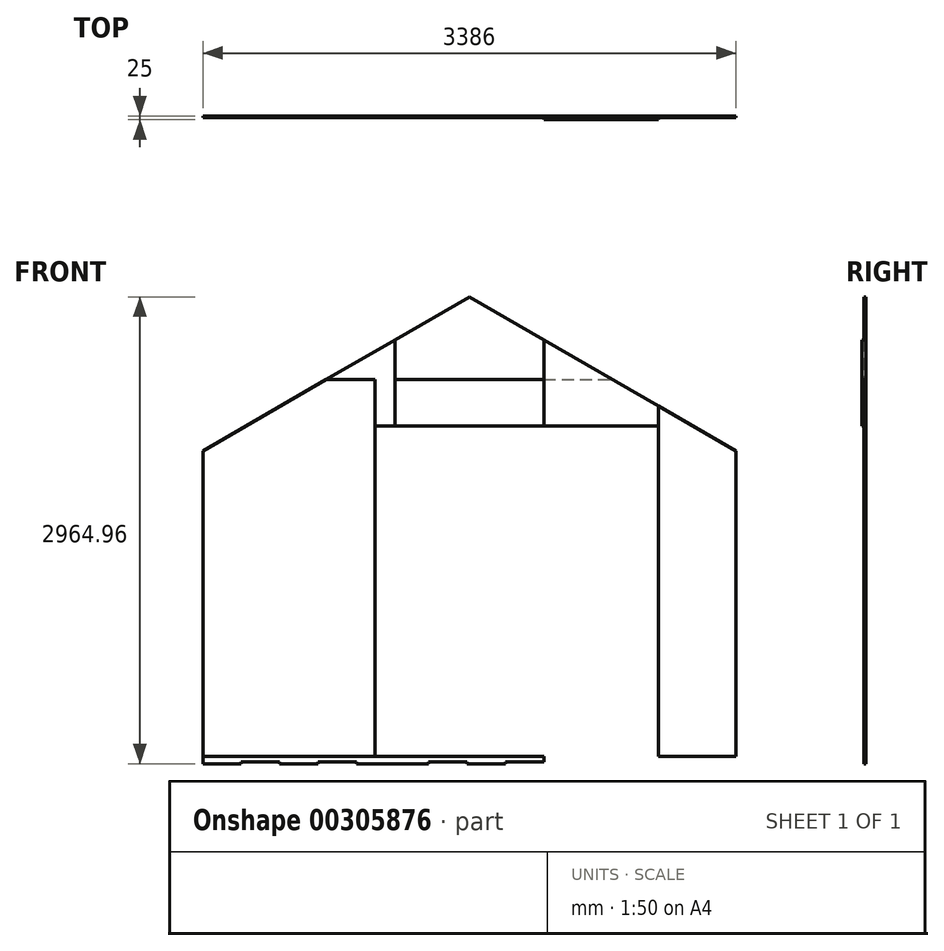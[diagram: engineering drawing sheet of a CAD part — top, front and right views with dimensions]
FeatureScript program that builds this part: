
annotation { "Feature Type Name" : "Feature", "Feature Type Description" : "" }
export const myFeature = defineFeature(function(context is Context, id is Id, definition is map)
    precondition{}
    {
        {
            var Q0;
            Q0=qCreatedBy(makeId("Front.planeOp"),FACE);
            var sketch = newSketch(context, id + "F0", { "sketchPlane" : qUnion([Q0])});
            skLineSegment(sketch, "E0", {"start": v(38.84, -625.32) * mm, "end": v(1258.84, -625.32) * mm});
            skLineSegment(sketch, "E1", {"start": v(1258.84, -625.32) * mm, "end": v(1258.84, 1362.19) * mm});
            skLineSegment(sketch, "E2", {"start": v(38.84, -625.32) * mm, "end": v(38.84, 1814.68) * mm});
            skLineSegment(sketch, "E3", {"start": v(1258.84, 1362.19) * mm, "end": v(475.1, 1814.68) * mm});
            skLineSegment(sketch, "E4", {"start": v(38.84, 1814.68) * mm, "end": v(475.1, 1814.68) * mm});
            skLineSegment(sketch, "E5.bottom", {"start": v(38.84, 1814.68) * mm, "end": v(-907.16, 1814.68) * mm});
            skLineSegment(sketch, "E5.top", {"start": v(38.84, -625.32) * mm, "end": v(-907.16, -625.32) * mm});
            skLineSegment(sketch, "E5.left", {"start": v(38.84, 1814.68) * mm, "end": v(38.84, -625.32) * mm});
            skLineSegment(sketch, "E5.right", {"start": v(-907.16, 1814.68) * mm, "end": v(-907.16, -625.32) * mm});
            skLineSegment(sketch, "E6", {"start": v(-434.16, 1814.68) * mm, "end": v(-434.16, 2602.28) * mm, "construction": true});
            skLineSegment(sketch, "E7", {"start": v(475.1, 1814.68) * mm, "end": v(-434.16, 2339.64) * mm});
            skPoint(sketch, "E7.endSnap0", {"position": v(-434.16, 2208.48) * mm});
            skLineSegment(sketch, "E8", {"start": v(-434.16, 2339.64) * mm, "end": v(-1343.42, 1814.68) * mm});
            skLineSegment(sketch, "E9", {"start": v(-907.16, 1814.68) * mm, "end": v(-907.16, 2066.55) * mm});
            skLineSegment(sketch, "E10", {"start": v(38.84, 1814.68) * mm, "end": v(38.84, 2066.55) * mm});
            skLineSegment(sketch, "E11", {"start": v(475.1, 1814.68) * mm, "end": v(475.1, -625.32) * mm, "construction": true});
            skLineSegment(sketch, "E12", {"start": v(1258.84, -625.32) * mm, "end": v(1014.84, -625.32) * mm});
            skLineSegment(sketch, "E13", {"start": v(1014.84, -625.32) * mm, "end": v(1014.84, -613.32) * mm});
            skLineSegment(sketch, "E14", {"start": v(1014.84, -613.32) * mm, "end": v(770.84, -613.32) * mm});
            skLineSegment(sketch, "E15", {"start": v(770.84, -613.32) * mm, "end": v(770.84, -625.32) * mm});
            skLineSegment(sketch, "E16", {"start": v(770.84, -625.32) * mm, "end": v(526.84, -625.32) * mm});
            skLineSegment(sketch, "E17", {"start": v(526.84, -625.32) * mm, "end": v(526.84, -613.32) * mm});
            skLineSegment(sketch, "E18", {"start": v(526.84, -613.32) * mm, "end": v(282.84, -613.32) * mm});
            skLineSegment(sketch, "E19", {"start": v(282.84, -613.32) * mm, "end": v(282.84, -625.32) * mm});
            skLineSegment(sketch, "E20", {"start": v(282.84, -625.32) * mm, "end": v(38.84, -625.32) * mm});
            skLineSegment(sketch, "E21", {"start": v(38.84, -625.32) * mm, "end": v(38.84, -613.32) * mm});
            skLineSegment(sketch, "E22", {"start": v(38.84, -613.32) * mm, "end": v(-205.16, -613.32) * mm});
            skLineSegment(sketch, "E23", {"start": v(-205.16, -613.32) * mm, "end": v(-205.16, -625.32) * mm});
            skLineSegment(sketch, "E24", {"start": v(-205.16, -625.32) * mm, "end": v(-449.16, -625.32) * mm});
            skLineSegment(sketch, "E25", {"start": v(-449.16, -625.32) * mm, "end": v(-449.16, -613.32) * mm});
            skLineSegment(sketch, "E26", {"start": v(-449.16, -613.32) * mm, "end": v(-693.16, -613.32) * mm});
            skLineSegment(sketch, "E27", {"start": v(-693.16, -613.32) * mm, "end": v(-693.16, -625.32) * mm});
            skLineSegment(sketch, "E28", {"start": v(-693.16, -625.32) * mm, "end": v(-907.16, -625.32) * mm});
            skLineSegment(sketch, "E29", {"start": v(-907.16, -625.32) * mm, "end": v(-2127.16, -625.32) * mm});
            skLineSegment(sketch, "E30.MirrorCS", {"start": v(-1343.42, 1814.68) * mm, "end": v(-434.16, 2339.64) * mm});
            skLineSegment(sketch, "E31.MirrorCS", {"start": v(-907.16, 1814.68) * mm, "end": v(-1343.42, 1814.68) * mm});
            skLineSegment(sketch, "E32.MirrorCS", {"start": v(-2127.16, 1362.19) * mm, "end": v(-1343.42, 1814.68) * mm});
            skLineSegment(sketch, "E33.MirrorCS", {"start": v(-1343.42, 1814.68) * mm, "end": v(-1343.42, -625.32) * mm, "construction": true});
            skLineSegment(sketch, "E34.MirrorCS", {"start": v(-2127.16, -625.32) * mm, "end": v(-2127.16, 1362.19) * mm});
            skLineSegment(sketch, "E35.MirrorCS", {"start": v(-1883.16, -625.32) * mm, "end": v(-1883.16, -613.32) * mm});
            skLineSegment(sketch, "E36.MirrorCS", {"start": v(-1883.16, -613.32) * mm, "end": v(-1639.16, -613.32) * mm});
            skLineSegment(sketch, "E37.MirrorCS", {"start": v(-1639.16, -613.32) * mm, "end": v(-1639.16, -625.32) * mm});
            skLineSegment(sketch, "E38.MirrorCS", {"start": v(-1395.16, -625.32) * mm, "end": v(-1395.16, -613.32) * mm});
            skLineSegment(sketch, "E39.MirrorCS", {"start": v(-1395.16, -613.32) * mm, "end": v(-1151.16, -613.32) * mm});
            skLineSegment(sketch, "E40.MirrorCS", {"start": v(-1151.16, -613.32) * mm, "end": v(-1151.16, -625.32) * mm});
            skLineSegment(sketch, "E41.MirrorCS", {"start": v(-1151.16, -625.32) * mm, "end": v(-907.16, -625.32) * mm});
            skLineSegment(sketch, "E42", {"start": v(-2127.16, -580.32) * mm, "end": v(1258.84, -580.32) * mm});
            skLineSegment(sketch, "E43", {"start": v(-434.16, -580.32) * mm, "end": v(-434.16, 1519.68) * mm, "construction": true});
            skLineSegment(sketch, "E44", {"start": v(-434.16, 1519.68) * mm, "end": v(-1034.16, 1519.68) * mm});
            skLineSegment(sketch, "E45", {"start": v(-1034.16, 1519.68) * mm, "end": v(-1034.16, -580.32) * mm});
            skLineSegment(sketch, "E46", {"start": v(-434.16, 1519.68) * mm, "end": v(765.84, 1519.68) * mm});
            skLineSegment(sketch, "E47", {"start": v(765.84, 1519.68) * mm, "end": v(765.84, -580.32) * mm});
            skLineSegment(sketch, "E48", {"start": v(-1034.16, 1519.68) * mm, "end": v(-1034.16, 1814.68) * mm});
            skLineSegment(sketch, "E49", {"start": v(765.84, 1519.68) * mm, "end": v(765.84, 1814.68) * mm});
            skSolve(sketch);
        }
        {
            var Q0;
            {var subQ5=sQuery(id+"F0.wireOp",EDGE,"E32.MirrorCS");Q0=makeQuery(id+"F0.imprint","IMPRINT",FACE,{"disambiguationData":[TD([[makeQuery(id+"F0.imprint","IMPRINT",EDGE,{"derivedFrom":subQ5}),-1.0]])]});}
            extrude(context, id + "F1", {"entities" : qUnion([Q0]), "depth" : 12 * mm});
        }
        {
            var Q0;
            {var subQ1=sQuery(id+"F0.wireOp",EDGE,"E3");Q0=makeQuery(id+"F0.imprint","IMPRINT",FACE,{"disambiguationData":[TD([[makeQuery(id+"F0.imprint","IMPRINT",EDGE,{"derivedFrom":subQ1}),1.0]])]});}
            extrude(context, id + "F2", {"entities" : qUnion([Q0]), "depth" : 12 * mm});
        }
        {
            var Q0;
            Q0=makeQuery(id+"F0.imprint","IMPRINT",FACE,{"disambiguationData":[TD([[makeQuery(id+"F0.imprint","IMPRINT",EDGE,{"derivedFrom":sQuery(id+"F0.wireOp",EDGE,"E5.bottom")}),-1.0]])]});
            extrude(context, id + "F3", {"entities" : qUnion([Q0]), "depth" : 12 * mm});
        }
        {
            var Q0;
            {var subQ1=sQuery(id+"F0.wireOp",EDGE,"E5.bottom");Q0=makeQuery(id+"F0.imprint","IMPRINT",FACE,{"disambiguationData":[TD([[makeQuery(id+"F0.imprint","IMPRINT",EDGE,{"derivedFrom":subQ1}),1.0]])]});}
            extrude(context, id + "F4", {"entities" : qUnion([Q0]), "depth" : 12 * mm});
        }
        {
            var Q0;
            {var subQ0=sQuery(id+"F0.wireOp",EDGE,"E9");Q0=makeQuery(id+"F0.imprint","IMPRINT",FACE,{"disambiguationData":[TD([[makeQuery(id+"F0.imprint","IMPRINT",EDGE,{"derivedFrom":subQ0}),1.0]])]});}
            var Q1;
            {var subQ3=sQuery(id+"F0.wireOp",EDGE,"E48");Q1=makeQuery(id+"F0.imprint","IMPRINT",FACE,{"disambiguationData":[TD([[makeQuery(id+"F0.imprint","IMPRINT",EDGE,{"derivedFrom":subQ3}),-1.0]])]});}
            extrude(context, id + "F5", {"entities" : qUnion([Q0, Q1]), "depth" : 12 * mm});
        }
        {
            var Q0;
            {var subQ0=sQuery(id+"F0.wireOp",EDGE,"E10");Q0=makeQuery(id+"F0.imprint","IMPRINT",FACE,{"disambiguationData":[TD([[makeQuery(id+"F0.imprint","IMPRINT",EDGE,{"derivedFrom":subQ0}),-1.0]])]});}
            var Q1;
            {var subQ3=sQuery(id+"F0.wireOp",EDGE,"E49");Q1=makeQuery(id+"F0.imprint","IMPRINT",FACE,{"disambiguationData":[TD([[makeQuery(id+"F0.imprint","IMPRINT",EDGE,{"derivedFrom":subQ3}),1.0]])]});}
            extrude(context, id + "F6", {"entities" : qUnion([Q0, Q1]), "depth" : 25 * mm});
        }
        {
            var Q0;
            {var subQ4=sQuery(id+"F0.wireOp",EDGE,"E35.MirrorCS");Q0=makeQuery(id+"F0.imprint","IMPRINT",FACE,{"disambiguationData":[TD([[makeQuery(id+"F0.imprint","IMPRINT",EDGE,{"derivedFrom":subQ4}),1.0]])]});}
            var Q1;
            {var subQ0=sQuery(id+"F0.wireOp",EDGE,"E22");Q1=makeQuery(id+"F0.imprint","IMPRINT",FACE,{"disambiguationData":[TD([[makeQuery(id+"F0.imprint","IMPRINT",EDGE,{"derivedFrom":subQ0}),-1.0]])]});}
            var Q2;
            {var subQ0=sQuery(id+"F0.wireOp",EDGE,"E12");Q2=makeQuery(id+"F0.imprint","IMPRINT",FACE,{"disambiguationData":[TD([[makeQuery(id+"F0.imprint","IMPRINT",EDGE,{"derivedFrom":subQ0}),-1.0]])]});}
            extrude(context, id + "F7", {"entities" : qUnion([Q0, Q1, Q2]), "depth" : 12 * mm});
        }
    });
